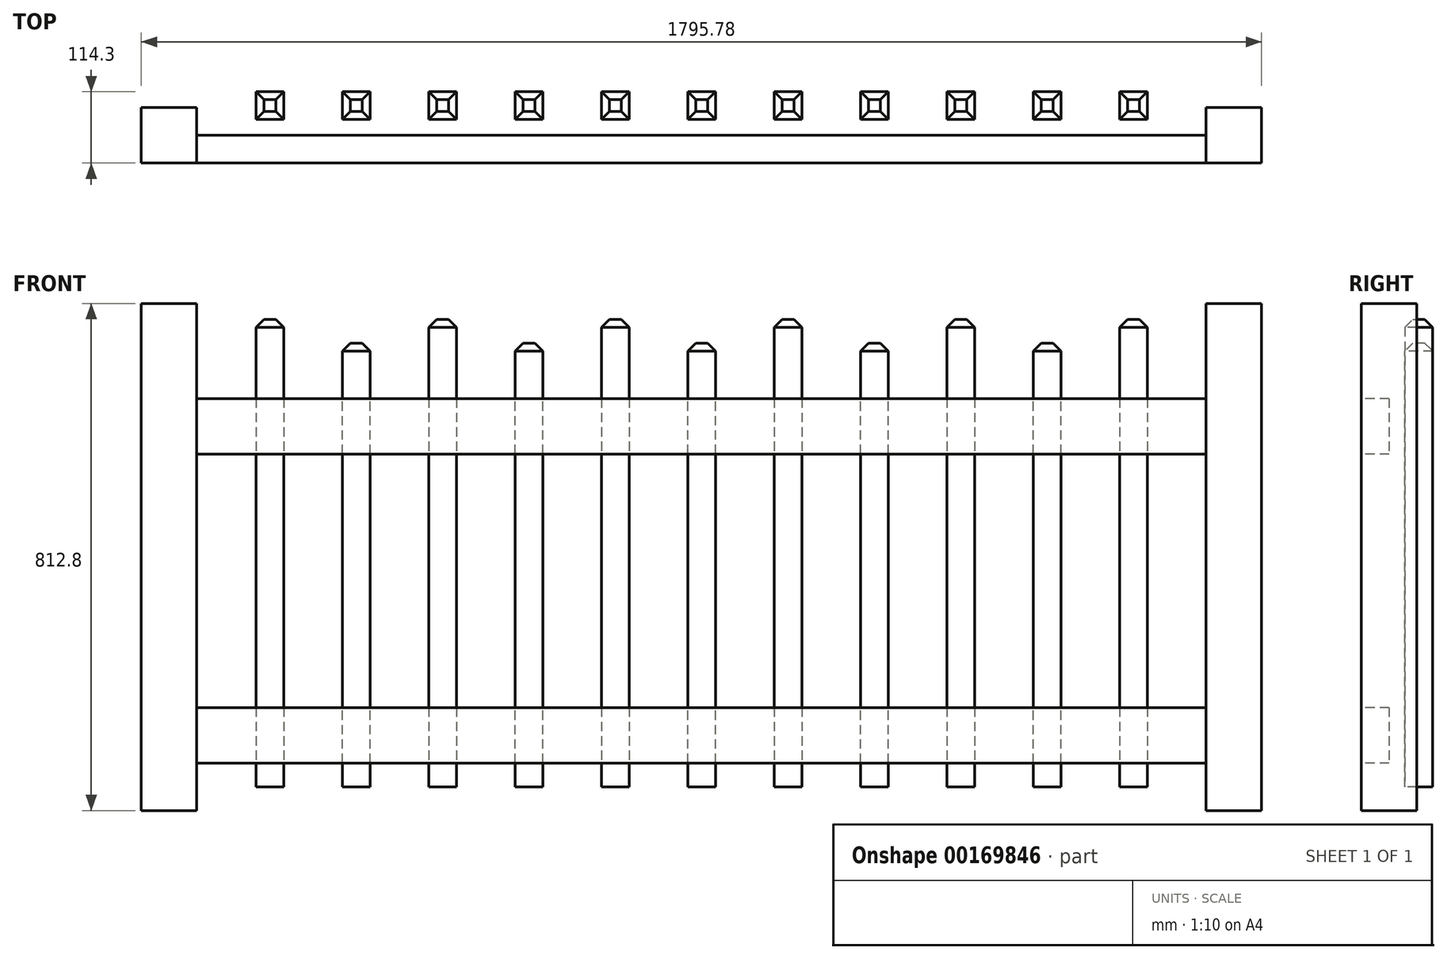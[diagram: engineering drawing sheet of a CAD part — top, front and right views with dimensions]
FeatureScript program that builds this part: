
annotation { "Feature Type Name" : "Feature", "Feature Type Description" : "" }
export const myFeature = defineFeature(function(context is Context, id is Id, definition is map)
    precondition{}
    {
        {
            var Q0;
            Q0=qCreatedBy(makeId("Top.planeOp"),FACE);
            var sketch = newSketch(context, id + "F0", { "sketchPlane" : qUnion([Q0])});
            skLineSegment(sketch, "E0.bottom", {"start": v(-1060.67, 0) * mm, "end": v(-971.77, 0) * mm});
            skLineSegment(sketch, "E0.top", {"start": v(-1060.67, 88.9) * mm, "end": v(-971.77, 88.9) * mm});
            skLineSegment(sketch, "E0.left", {"start": v(-1060.67, 0) * mm, "end": v(-1060.67, 88.9) * mm});
            skLineSegment(sketch, "E0.right", {"start": v(-971.77, 0) * mm, "end": v(-971.77, 88.9) * mm});
            skLineSegment(sketch, "E1.bottom", {"start": v(646.21, 0) * mm, "end": v(735.11, 0) * mm});
            skLineSegment(sketch, "E1.top", {"start": v(646.21, 88.9) * mm, "end": v(735.11, 88.9) * mm});
            skLineSegment(sketch, "E1.left", {"start": v(646.21, 0) * mm, "end": v(646.21, 88.9) * mm});
            skLineSegment(sketch, "E1.right", {"start": v(735.11, 0) * mm, "end": v(735.11, 88.9) * mm});
            skSolve(sketch);
        }
        {
            var Q0;
            Q0 = qSketchRegion(id + "F0", true);
            extrude(context, id + "F1", {"entities" : qUnion([Q0]), "depth" : 812.8 * mm});
        }
        {
            var Q0;
            Q0=qCreatedBy(makeId("Top.planeOp"),FACE);
            var sketch = newSketch(context, id + "F2", { "sketchPlane" : qUnion([Q0])});
            skLineSegment(sketch, "E2.bottom", {"start": v(-1454.99, 786.33) * mm, "end": v(1416.69, 786.33) * mm});
            skLineSegment(sketch, "E2.top", {"start": v(-1454.99, -891.52) * mm, "end": v(1416.69, -891.52) * mm});
            skLineSegment(sketch, "E2.left", {"start": v(-1454.99, 786.33) * mm, "end": v(-1454.99, -891.52) * mm});
            skLineSegment(sketch, "E2.right", {"start": v(1416.69, 786.33) * mm, "end": v(1416.69, -891.52) * mm});
            skSolve(sketch);
        }
        {
            var Q0;
            Q0=qCreatedBy(makeId("Front.planeOp"),FACE);
            cPlane(context, id + "F3", {"entities" : qUnion([Q0]), "cplaneType" : CPlaneType.OFFSET, "offset" : 0 * mm, "oppositeDirection" : true, "width" : 152.4 * mm, "height" : 152.4 * mm});
        }
        {
            var Q0;
            Q0=qCreatedBy(id+"F3.planeOp",FACE);
            var sketch = newSketch(context, id + "F4", { "sketchPlane" : qUnion([Q0])});
            skLineSegment(sketch, "E3.bottom", {"start": v(-971.77, 660.4) * mm, "end": v(646.21, 660.4) * mm});
            skLineSegment(sketch, "E3.top", {"start": v(-971.77, 571.5) * mm, "end": v(646.21, 571.5) * mm});
            skLineSegment(sketch, "E3.left", {"start": v(-971.77, 660.4) * mm, "end": v(-971.77, 571.5) * mm});
            skLineSegment(sketch, "E3.right", {"start": v(646.21, 660.4) * mm, "end": v(646.21, 571.5) * mm});
            skLineSegment(sketch, "E4.bottom", {"start": v(-971.77, 165.1) * mm, "end": v(646.21, 165.1) * mm});
            skLineSegment(sketch, "E4.top", {"start": v(-971.77, 76.2) * mm, "end": v(646.21, 76.2) * mm});
            skLineSegment(sketch, "E4.left", {"start": v(-971.77, 165.1) * mm, "end": v(-971.77, 76.2) * mm});
            skLineSegment(sketch, "E4.right", {"start": v(646.21, 165.1) * mm, "end": v(646.21, 76.2) * mm});
            skSolve(sketch);
        }
        {
            var Q0;
            Q0 = qSketchRegion(id + "F4", true);
            extrude(context, id + "F5", {"entities" : qUnion([Q0]), "oppositeDirection" : true, "depth" : 44.45 * mm});
        }
        {
            var Q0;
            Q0=makeQuery(id+"F5.opExtrude","CAP_FACE",FACE,{"disambiguationData":[OSD([sQuery(id+"F4.wireOp",EDGE,"E3.bottom"),sQuery(id+"F4.wireOp",EDGE,"E3.top"),sQuery(id+"F4.wireOp",EDGE,"E3.left"),sQuery(id+"F4.wireOp",EDGE,"E3.right")])],"isStart":false});
            cPlane(context, id + "F6", {"entities" : qUnion([Q0]), "cplaneType" : CPlaneType.OFFSET, "offset" : 25.4 * mm, "width" : 152.4 * mm, "height" : 152.4 * mm});
        }
        {
            var Q0;
            Q0=makeQuery(id+"F1.opExtrude","SWEPT_FACE",FACE,{"disambiguationData":[OSD([sQuery(id+"F0.wireOp",EDGE,"E1.left")])]});
            cPlane(context, id + "F7", {"entities" : qUnion([Q0]), "cplaneType" : CPlaneType.OFFSET, "offset" : 0 * mm, "width" : 152.4 * mm, "height" : 152.4 * mm});
        }
        {
            var Q0;
            Q0=qCreatedBy(id+"F6.planeOp",FACE);
            var sketch = newSketch(context, id + "F8", { "sketchPlane" : qUnion([Q0])});
            skLineSegment(sketch, "E5.bottom", {"start": v(-552.23, 787.4) * mm, "end": v(-507.78, 787.4) * mm});
            skLineSegment(sketch, "E5.top", {"start": v(-552.23, 38.1) * mm, "end": v(-507.78, 38.1) * mm});
            skLineSegment(sketch, "E5.left", {"start": v(-552.23, 787.4) * mm, "end": v(-552.23, 38.1) * mm});
            skLineSegment(sketch, "E5.right", {"start": v(-507.78, 787.4) * mm, "end": v(-507.78, 38.1) * mm});
            skLineSegment(sketch, "E6.1.0.0", {"start": v(-275.37, 787.4) * mm, "end": v(-275.37, 38.1) * mm});
            skLineSegment(sketch, "E6.1.0.1", {"start": v(-230.92, 787.4) * mm, "end": v(-230.92, 38.1) * mm});
            skLineSegment(sketch, "E6.1.0.2", {"start": v(-275.37, 787.4) * mm, "end": v(-230.92, 787.4) * mm});
            skLineSegment(sketch, "E6.1.0.3", {"start": v(-275.37, 38.1) * mm, "end": v(-230.92, 38.1) * mm});
            skLineSegment(sketch, "E6.2.0.0", {"start": v(1.49, 787.4) * mm, "end": v(1.49, 38.1) * mm});
            skLineSegment(sketch, "E6.2.0.1", {"start": v(45.94, 787.4) * mm, "end": v(45.94, 38.1) * mm});
            skLineSegment(sketch, "E6.2.0.2", {"start": v(1.49, 787.4) * mm, "end": v(45.94, 787.4) * mm});
            skLineSegment(sketch, "E6.2.0.3", {"start": v(1.49, 38.1) * mm, "end": v(45.94, 38.1) * mm});
            skLineSegment(sketch, "E6.3.0.0", {"start": v(278.35, 787.4) * mm, "end": v(278.35, 38.1) * mm});
            skLineSegment(sketch, "E6.3.0.1", {"start": v(322.8, 787.4) * mm, "end": v(322.8, 38.1) * mm});
            skLineSegment(sketch, "E6.3.0.2", {"start": v(278.35, 787.4) * mm, "end": v(322.8, 787.4) * mm});
            skLineSegment(sketch, "E6.3.0.3", {"start": v(278.35, 38.1) * mm, "end": v(322.8, 38.1) * mm});
            skLineSegment(sketch, "E6.4.0.0", {"start": v(555.2, 787.4) * mm, "end": v(555.2, 38.1) * mm});
            skLineSegment(sketch, "E6.4.0.1", {"start": v(599.66, 787.4) * mm, "end": v(599.66, 38.1) * mm});
            skLineSegment(sketch, "E6.4.0.2", {"start": v(555.2, 787.4) * mm, "end": v(599.66, 787.4) * mm});
            skLineSegment(sketch, "E6.4.0.3", {"start": v(555.2, 38.1) * mm, "end": v(599.66, 38.1) * mm});
            skLineSegment(sketch, "E6.5.0.0", {"start": v(832.07, 787.4) * mm, "end": v(832.07, 38.1) * mm});
            skLineSegment(sketch, "E6.5.0.1", {"start": v(876.52, 787.4) * mm, "end": v(876.52, 38.1) * mm});
            skLineSegment(sketch, "E6.5.0.2", {"start": v(832.07, 787.4) * mm, "end": v(876.52, 787.4) * mm});
            skLineSegment(sketch, "E6.5.0.3", {"start": v(832.07, 38.1) * mm, "end": v(876.52, 38.1) * mm});
            skLineSegment(sketch, "E6.direction1", {"start": v(-541.98, 38.1) * mm, "end": v(-265.12, 38.1) * mm, "construction": true});
            skSolve(sketch);
        }
        {
            var Q0;
            Q0 = qSketchRegion(id + "F8", true);
            extrude(context, id + "F9", {"entities" : qUnion([Q0]), "depth" : 44.45 * mm});
        }
        {
            var Q0;
            Q0=qCreatedBy(id+"F6.planeOp",FACE);
            var sketch = newSketch(context, id + "F10", { "sketchPlane" : qUnion([Q0])});
            skLineSegment(sketch, "E7.bottom", {"start": v(-413.55, 38.1) * mm, "end": v(-369.1, 38.1) * mm});
            skLineSegment(sketch, "E7.top", {"start": v(-413.55, 749.3) * mm, "end": v(-369.1, 749.3) * mm});
            skLineSegment(sketch, "E7.left", {"start": v(-413.55, 38.1) * mm, "end": v(-413.55, 749.3) * mm});
            skLineSegment(sketch, "E7.right", {"start": v(-369.1, 38.1) * mm, "end": v(-369.1, 749.3) * mm});
            skLineSegment(sketch, "E8.1.0.0", {"start": v(-136.69, 38.1) * mm, "end": v(-136.69, 749.3) * mm});
            skLineSegment(sketch, "E8.1.0.1", {"start": v(-136.69, 749.3) * mm, "end": v(-92.24, 749.3) * mm});
            skLineSegment(sketch, "E8.1.0.2", {"start": v(-92.24, 38.1) * mm, "end": v(-92.24, 749.3) * mm});
            skLineSegment(sketch, "E8.1.0.3", {"start": v(-136.69, 38.1) * mm, "end": v(-92.24, 38.1) * mm});
            skLineSegment(sketch, "E8.2.0.0", {"start": v(140.17, 38.1) * mm, "end": v(140.17, 749.3) * mm});
            skLineSegment(sketch, "E8.2.0.1", {"start": v(140.17, 749.3) * mm, "end": v(184.62, 749.3) * mm});
            skLineSegment(sketch, "E8.2.0.2", {"start": v(184.62, 38.1) * mm, "end": v(184.62, 749.3) * mm});
            skLineSegment(sketch, "E8.2.0.3", {"start": v(140.17, 38.1) * mm, "end": v(184.62, 38.1) * mm});
            skLineSegment(sketch, "E8.3.0.0", {"start": v(417.03, 38.1) * mm, "end": v(417.03, 749.3) * mm});
            skLineSegment(sketch, "E8.3.0.1", {"start": v(417.03, 749.3) * mm, "end": v(461.48, 749.3) * mm});
            skLineSegment(sketch, "E8.3.0.2", {"start": v(461.48, 38.1) * mm, "end": v(461.48, 749.3) * mm});
            skLineSegment(sketch, "E8.3.0.3", {"start": v(417.03, 38.1) * mm, "end": v(461.48, 38.1) * mm});
            skLineSegment(sketch, "E8.4.0.0", {"start": v(693.9, 38.1) * mm, "end": v(693.9, 749.3) * mm});
            skLineSegment(sketch, "E8.4.0.1", {"start": v(693.9, 749.3) * mm, "end": v(738.34, 749.3) * mm});
            skLineSegment(sketch, "E8.4.0.2", {"start": v(738.34, 38.1) * mm, "end": v(738.34, 749.3) * mm});
            skLineSegment(sketch, "E8.4.0.3", {"start": v(693.9, 38.1) * mm, "end": v(738.34, 38.1) * mm});
            skLineSegment(sketch, "E8.direction1", {"start": v(-413.55, 38.1) * mm, "end": v(-136.69, 38.1) * mm, "construction": true});
            skSolve(sketch);
        }
        {
            var Q0;
            Q0 = qSketchRegion(id + "F10", true);
            extrude(context, id + "F11", {"entities" : qUnion([Q0]), "depth" : 44.45 * mm});
        }
        {
            var Q0;
            Q0=makeQuery(id+"F9.opExtrude","SWEPT_FACE",FACE,{"disambiguationData":[OSD([sQuery(id+"F8.wireOp",EDGE,"E5.bottom")])]});
            var Q1;
            Q1=makeQuery(id+"F11.opExtrude","SWEPT_FACE",FACE,{"disambiguationData":[OSD([sQuery(id+"F10.wireOp",EDGE,"E7.top")])]});
            var Q2;
            Q2=makeQuery(id+"F9.opExtrude","SWEPT_FACE",FACE,{"disambiguationData":[OSD([sQuery(id+"F8.wireOp",EDGE,"E6.1.0.2")])]});
            var Q3;
            Q3=makeQuery(id+"F11.opExtrude","SWEPT_FACE",FACE,{"disambiguationData":[OSD([sQuery(id+"F10.wireOp",EDGE,"E8.1.0.1")])]});
            var Q4;
            Q4=makeQuery(id+"F9.opExtrude","SWEPT_FACE",FACE,{"disambiguationData":[OSD([sQuery(id+"F8.wireOp",EDGE,"E6.2.0.2")])]});
            var Q5;
            Q5=makeQuery(id+"F11.opExtrude","SWEPT_FACE",FACE,{"disambiguationData":[OSD([sQuery(id+"F10.wireOp",EDGE,"E8.2.0.1")])]});
            var Q6;
            Q6=makeQuery(id+"F9.opExtrude","SWEPT_FACE",FACE,{"disambiguationData":[OSD([sQuery(id+"F8.wireOp",EDGE,"E6.3.0.2")])]});
            var Q7;
            Q7=makeQuery(id+"F11.opExtrude","SWEPT_FACE",FACE,{"disambiguationData":[OSD([sQuery(id+"F10.wireOp",EDGE,"E8.3.0.1")])]});
            var Q8;
            Q8=makeQuery(id+"F9.opExtrude","SWEPT_FACE",FACE,{"disambiguationData":[OSD([sQuery(id+"F8.wireOp",EDGE,"E6.4.0.2")])]});
            var Q9;
            Q9=makeQuery(id+"F11.opExtrude","SWEPT_FACE",FACE,{"disambiguationData":[OSD([sQuery(id+"F10.wireOp",EDGE,"E8.4.0.1")])]});
            var Q10;
            Q10=makeQuery(id+"F9.opExtrude","SWEPT_FACE",FACE,{"disambiguationData":[OSD([sQuery(id+"F8.wireOp",EDGE,"E6.5.0.2")])]});
            chamfer(context, id + "F12", {"entities" : qUnion([Q0, Q1, Q2, Q3, Q4, Q5, Q6, Q7, Q8, Q9, Q10]), "width" : 12.7 * mm, "tangentPropagation" : true});
        }
    });
